# Revit family: 58162071
name_source: partatom
category: Plumbing Fixtures
revit_build: Autodesk Revit 2016 (Build: 20150714_1515(x64)
units: mm (PartAtom-declared; Revit-internal decimal feet)

## family parameters
Always vertical = Yes
Cut with Voids When Loaded = No
OmniClass Number = 23.45.55.00
OmniClass Title = Sanitary Faucets, Wastes
Part Type = Normal
Room Calculation Point = No
Round Connector Dimension = Use Diameter
Shared = No
Work Plane-Based = No

## types (1)
- 58162071 Bath and shower faucet
    2D/3D/BIM Files URL = http://static.hansa.com
    Aerator = Aerator
    AssetType = Fixed
    BIMObjectName = 58162071
    BodyMaterial = Brass
    Brand = Hansa
    Catalog Drawing URL = http://static.hansa.com
    Category = Bathroom, shower
    Class = Thermostatic
    CloseOffRating = 0
    Color = Chrome
    Connection = Without eccentric union
    Constituents = Temperature and volume control, diverter, EcoFlow control
    ConvergoRefNr = 0087-1809-0168-FI
    Customs Code = 84818011
    DN Size = DN15
    Description = Thermostatic shower faucet with spout
    Dimension Drawing URL = http://static.hansa.com
    Diverter = Integrated diverter / Volume control
    DurationUnit = Year
    EAN Number = 4057304003479
    FDV Document URL = http://www.hansa.com
    FaucetMainMaterial = Brass
    Features = Thermostatic
    Finish = Polished
    Flow = EcoFlow control
    Flow Drawing URL = http://static.hansa.com
    Flow Rate At 300kPa = 0.3 L/s
    FlowCoefficient = 0
    Group = Bath and shower faucets
    IfcExportAs = IfcValveType
    IfcExportType = FAUCET
    Installation Type = Wall-mounted
    Installation Width = cc150 mm
    Installation and Maintenance = http://static.hansa.com
    Lever Handle = Flow control handle
    ManufacterURL = http://www.hansa.com
    Manufacturer = Hansa
    ManufacturerName = Hansa
    Market = BEL;CZE;ESP;FRA;INT;ITA;NLD;SVK
    Material = Brass
    Mechanical Parts = Litter filter(s); Pressure plug; Ceramic head part
    Model = 58162071 Bath and shower faucet
    ModelReference = 58162071
    NBSDescription = Water supply fittings for baths
    NBSReference = 45-35-70/315
    Name = 58162071 Bath and shower faucet
    Name_en = 58162071 Bath and shower faucet
    Noise Class = II (ISO 3822) Oras lab.
    NominalDepth = 152 mm  [stored 0.498688 ft]
    NominalHeight = 72 mm  [stored 0.23622 ft]
    NominalWidth = 290 mm  [stored 0.951444 ft]
    Package Weight = 1.73 kg
    Package external Dimensions = 294 x 164 x 83
    Product Code = 58162071
    Product Datasheet = http://www.hansa.com
    Product Family = HANSAMICRA
    Product Image URL = http://static.hansa.com
    Product URL = http://static.hansa.com
    ProductInformation = Thermostatic shower faucet with spout
    Projection = 159 mm
    Revision = 2
    Safety Sales Arguments = THERMO COOL. Improved safety – the housing of the fittings conducts minimal heat.
    Shape = Sculptured
    Size = 290x152x72 mm
    Spare Parts = http://static.hansa.com
    Technology Sales Arguments = Suitable for instantaneous water heaters (shower above 20 kW or bathtub
    Temperature = Thermostatic temperature control; Thermostatic safety stop at 38°C
    Uniclass2 = Pr_40_30_96_78
    Uniclass2015Description = Shower manual water supply sets
    Uniclass2015Reference = Pr_40_20_87_78
    Version = 2
    VersionDate = 01/01/2019
    WarrantyDescription = http://warranty.hansa.com
    WarrantyDurationUnit = Year

note: [stored X ft] marks values corroborated as IEEE doubles in the binary element streams (Revit-internal decimal feet)

## geometry (parser evidence)
native form markers: Sweep x3
no freeform markers — native parametric forms only
